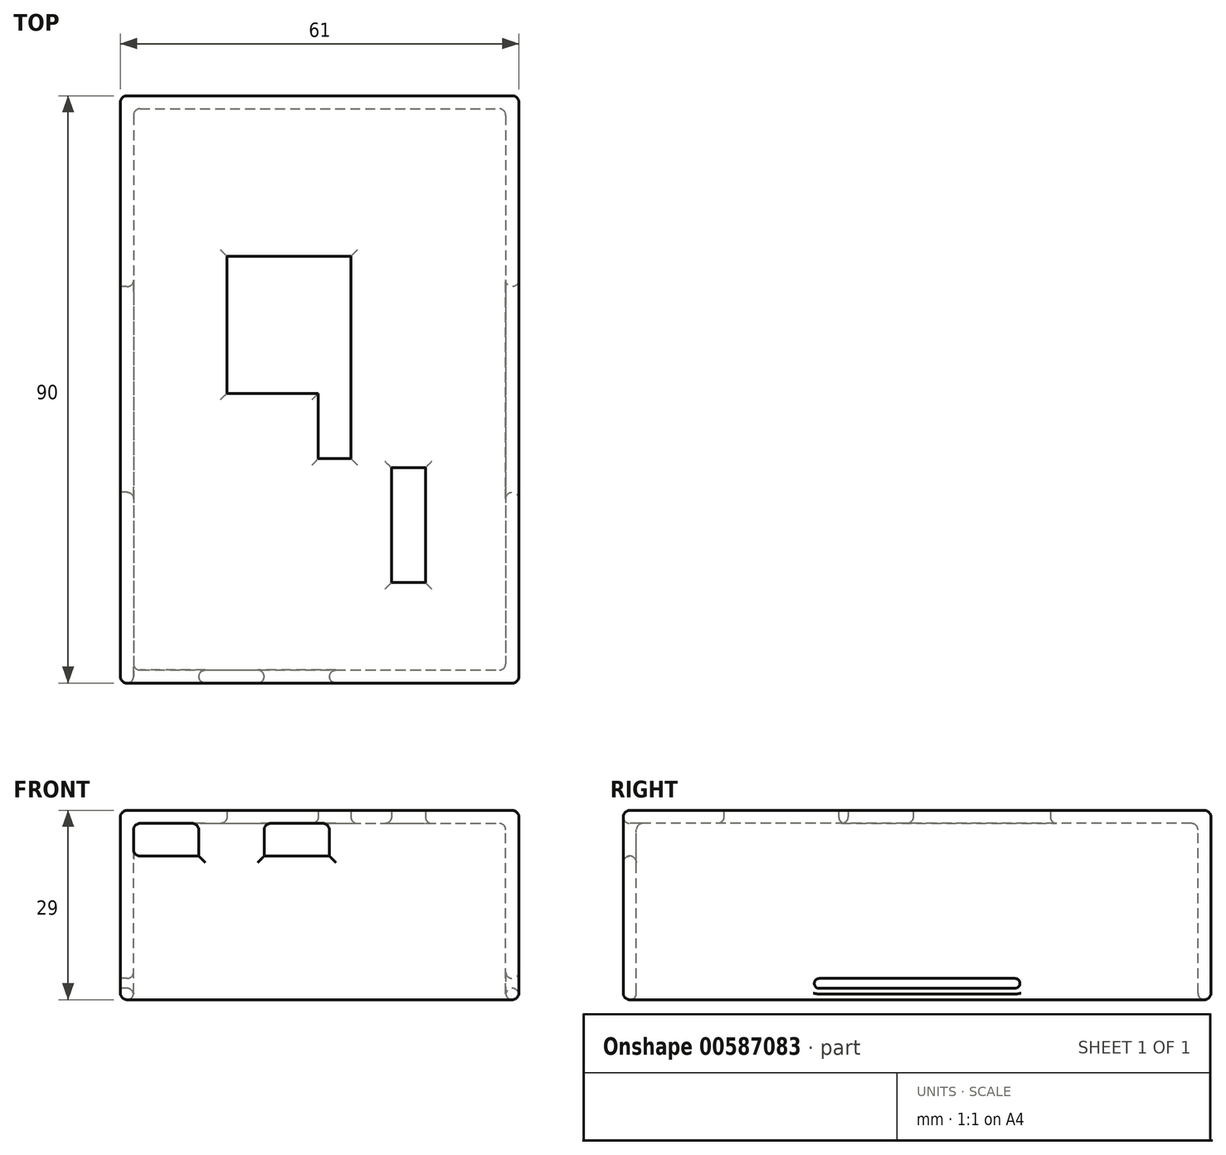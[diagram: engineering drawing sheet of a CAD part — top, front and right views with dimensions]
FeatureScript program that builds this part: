
annotation { "Feature Type Name" : "Feature", "Feature Type Description" : "" }
export const myFeature = defineFeature(function(context is Context, id is Id, definition is map)
    precondition{}
    {
        {
            var Q0;
            Q0=qCreatedBy(makeId("Top.planeOp"),FACE);
            var sketch = newSketch(context, id + "F0", { "sketchPlane" : qUnion([Q0])});
            skLineSegment(sketch, "E0.bottom", {"start": v(0, 0) * mm, "end": v(57, 0) * mm});
            skLineSegment(sketch, "E0.top", {"start": v(0, -86) * mm, "end": v(57, -86) * mm});
            skLineSegment(sketch, "E0.left", {"start": v(0, 0) * mm, "end": v(0, -86) * mm});
            skLineSegment(sketch, "E0.right", {"start": v(57, 0) * mm, "end": v(57, -86) * mm});
            skLineSegment(sketch, "E1.bottom", {"start": v(14.3, -22.6) * mm, "end": v(33.3, -22.6) * mm});
            skLineSegment(sketch, "E1.left", {"start": v(14.3, -22.6) * mm, "end": v(14.3, -43.6) * mm});
            skLineSegment(sketch, "E1.right", {"start": v(33.3, -22.6) * mm, "end": v(33.3, -43.6) * mm});
            skLineSegment(sketch, "E2", {"start": v(14.3, -22.6) * mm, "end": v(14.3, 0) * mm, "construction": true});
            skLineSegment(sketch, "E3", {"start": v(14.3, 0) * mm, "end": v(14.3, -22.6) * mm, "construction": true});
            skLineSegment(sketch, "E4", {"start": v(14.3, -22.6) * mm, "end": v(0, -22.6) * mm, "construction": true});
            skLineSegment(sketch, "E5.bottom", {"start": v(39.5, -55) * mm, "end": v(44.7, -55) * mm});
            skLineSegment(sketch, "E5.top", {"start": v(39.5, -72.6) * mm, "end": v(44.7, -72.6) * mm});
            skLineSegment(sketch, "E5.left", {"start": v(39.5, -55) * mm, "end": v(39.5, -72.6) * mm});
            skLineSegment(sketch, "E5.right", {"start": v(44.7, -55) * mm, "end": v(44.7, -72.6) * mm});
            skLineSegment(sketch, "E6", {"start": v(28.3, -43.6) * mm, "end": v(28.3, -53.6) * mm});
            skLineSegment(sketch, "E7", {"start": v(28.3, -53.6) * mm, "end": v(33.3, -53.6) * mm});
            skLineSegment(sketch, "E8", {"start": v(33.3, -53.6) * mm, "end": v(33.3, -43.6) * mm});
            skLineSegment(sketch, "E9", {"start": v(14.3, -43.6) * mm, "end": v(28.3, -43.6) * mm});
            skLineSegment(sketch, "E10", {"start": v(33.3, -43.6) * mm, "end": v(28.3, -43.6) * mm, "construction": true});
            skSolve(sketch);
        }
        {
            var Q0;
            Q0 = qSketchRegion(id + "F0", true);
            extrude(context, id + "F1", {"entities" : qUnion([Q0]), "depth" : 2 * mm, "offsetDistance" : 25 * mm});
        }
        {
            var Q0;
            Q0=makeQuery(id+"F1.opExtrude","CAP_FACE",FACE,{"disambiguationData":[OSD([sQuery(id+"F0.wireOp",EDGE,"E0.bottom"),sQuery(id+"F0.wireOp",EDGE,"E0.top"),sQuery(id+"F0.wireOp",EDGE,"E0.left"),sQuery(id+"F0.wireOp",EDGE,"E0.right"),sQuery(id+"F0.wireOp",EDGE,"E1.bottom"),sQuery(id+"F0.wireOp",EDGE,"E1.left"),sQuery(id+"F0.wireOp",EDGE,"E1.right"),sQuery(id+"F0.wireOp",EDGE,"E5.bottom"),sQuery(id+"F0.wireOp",EDGE,"E5.top"),sQuery(id+"F0.wireOp",EDGE,"E5.left"),sQuery(id+"F0.wireOp",EDGE,"E5.right"),sQuery(id+"F0.wireOp",EDGE,"E6"),sQuery(id+"F0.wireOp",EDGE,"E7"),sQuery(id+"F0.wireOp",EDGE,"E8"),sQuery(id+"F0.wireOp",EDGE,"E9")])],"isStart":false});
            var sketch = newSketch(context, id + "F2", { "sketchPlane" : qUnion([Q0])});
            skLineSegment(sketch, "E11.0", {"start": v(0, 0) * mm, "end": v(57, 0) * mm});
            skLineSegment(sketch, "E11.1", {"start": v(57, 0) * mm, "end": v(57, -86) * mm});
            skLineSegment(sketch, "E11.2", {"start": v(0, -86) * mm, "end": v(57, -86) * mm});
            skLineSegment(sketch, "E11.3", {"start": v(0, 0) * mm, "end": v(0, -86) * mm});
            skLineSegment(sketch, "E12.0", {"start": v(-2, 2) * mm, "end": v(59, 2) * mm});
            skLineSegment(sketch, "E12.1", {"start": v(-2, 2) * mm, "end": v(-2, -88) * mm});
            skLineSegment(sketch, "E12.2", {"start": v(-2, -88) * mm, "end": v(59, -88) * mm});
            skLineSegment(sketch, "E12.3", {"start": v(59, 2) * mm, "end": v(59, -88) * mm});
            skSolve(sketch);
        }
        {
            var Q0;
            Q0 = qSketchRegion(id + "F2", true);
            extrude(context, id + "F3", {"entities" : qUnion([Q0]), "operationType" : NewBodyOperationType.ADD, "oppositeDirection" : true, "depth" : 29 * mm, "offsetDistance" : 25 * mm});
        }
        {
            var Q0;
            Q0=makeQuery(id+"F3.opExtrude","SWEPT_FACE",FACE,{"disambiguationData":[OSD([sQuery(id+"F2.wireOp",EDGE,"E12.2")])]});
            var sketch = newSketch(context, id + "F4", { "sketchPlane" : qUnion([Q0])});
            skLineSegment(sketch, "E13.bottom", {"start": v(20, 0) * mm, "end": v(30, 0) * mm});
            skLineSegment(sketch, "E13.top", {"start": v(20, -5) * mm, "end": v(30, -5) * mm});
            skLineSegment(sketch, "E13.left", {"start": v(20, 0) * mm, "end": v(20, -5) * mm});
            skLineSegment(sketch, "E13.right", {"start": v(30, 0) * mm, "end": v(30, -5) * mm});
            skLineSegment(sketch, "E14.bottom", {"start": v(0, 0) * mm, "end": v(10, 0) * mm});
            skLineSegment(sketch, "E14.top", {"start": v(0, -5) * mm, "end": v(10, -5) * mm});
            skLineSegment(sketch, "E14.left", {"start": v(0, 0) * mm, "end": v(0, -5) * mm});
            skLineSegment(sketch, "E14.right", {"start": v(10, 0) * mm, "end": v(10, -5) * mm});
            skSolve(sketch);
        }
        {
            var Q0;
            Q0=makeQuery(id+"F4.imprint","IMPRINT",FACE,{"disambiguationData":[TD([[makeQuery(id+"F4.imprint","IMPRINT",EDGE,{"derivedFrom":sQuery(id+"F4.wireOp",EDGE,"E14.bottom")}),-1.0]])]});
            var Q1;
            Q1=makeQuery(id+"F4.imprint","IMPRINT",FACE,{"disambiguationData":[TD([[makeQuery(id+"F4.imprint","IMPRINT",EDGE,{"derivedFrom":sQuery(id+"F4.wireOp",EDGE,"E13.bottom")}),-1.0]])]});
            extrude(context, id + "F5", {"entities" : qUnion([Q0, Q1]), "operationType" : NewBodyOperationType.REMOVE, "endBound" : BoundingType.UP_TO_NEXT, "oppositeDirection" : true, "depth" : 25 * mm, "offsetDistance" : 25 * mm});
        }
        {
            var Q0;
            Q0=makeQuery(id+"F3.opExtrude","SWEPT_FACE",FACE,{"disambiguationData":[OSD([sQuery(id+"F2.wireOp",EDGE,"E12.1")])]});
            var sketch = newSketch(context, id + "F6", { "sketchPlane" : qUnion([Q0])});
            skLineSegment(sketch, "E15", {"start": v(43, -27) * mm, "end": v(43, -24.5) * mm, "construction": true});
            skLineSegment(sketch, "E16", {"start": v(28, -24.5) * mm, "end": v(58, -24.5) * mm, "construction": true});
            skArc(sketch, "E17.0.startCap", {"start": v(28, -25.25) * mm, "mid": v(27.25, -24.5) * mm, "end": v(28, -23.75) * mm});
            skArc(sketch, "E17.0.endCap", {"start": v(58, -23.75) * mm, "mid": v(58.75, -24.5) * mm, "end": v(58, -25.25) * mm});
            skLineSegment(sketch, "E17.0.left", {"start": v(28, -23.75) * mm, "end": v(58, -23.75) * mm});
            skLineSegment(sketch, "E17.0.right", {"start": v(28, -25.25) * mm, "end": v(58, -25.25) * mm});
            skSolve(sketch);
        }
        {
            var Q0;
            Q0 = qSketchRegion(id + "F6", true);
            extrude(context, id + "F7", {"entities" : qUnion([Q0]), "operationType" : NewBodyOperationType.REMOVE, "endBound" : BoundingType.THROUGH_ALL, "oppositeDirection" : true, "depth" : 25 * mm, "offsetDistance" : 25 * mm});
        }
        {
            var Q0;
            Q0=makeQuery(id+"F3.opExtrude","SWEPT_EDGE",EDGE,{"disambiguationData":[OSD([sQuery(id+"F2.wireOp",EDGE,"E12.1"),sQuery(id+"F2.wireOp",EDGE,"E12.2")])]});
            fillet(context, id + "F8", {"entities" : qUnion([Q0]), "radius" : 1 * mm, "tangentPropagation" : true, "allowEdgeOverflow" : false});
        }
        {
            var Q0;
            Q0=makeQuery(id+"F3.opExtrude","SWEPT_FACE",FACE,{"disambiguationData":[OSD([sQuery(id+"F2.wireOp",EDGE,"E12.2")])]});
            var Q1;
            Q1=makeQuery(id+"F3.opExtrude","SWEPT_FACE",FACE,{"disambiguationData":[OSD([sQuery(id+"F2.wireOp",EDGE,"E12.3")])]});
            var Q2;
            Q2=makeQuery(id+"F3.opExtrude","SWEPT_FACE",FACE,{"disambiguationData":[OSD([sQuery(id+"F2.wireOp",EDGE,"E12.0")])]});
            var Q3;
            Q3=makeQuery(id+"F5.boolean.opBoolean","MERGE",FACE,{"derivedFrom":[makeQuery(id+"F1.opExtrude","CAP_FACE",FACE,{"disambiguationData":[OSD([sQuery(id+"F0.wireOp",EDGE,"E0.bottom"),sQuery(id+"F0.wireOp",EDGE,"E0.top"),sQuery(id+"F0.wireOp",EDGE,"E0.left"),sQuery(id+"F0.wireOp",EDGE,"E0.right"),sQuery(id+"F0.wireOp",EDGE,"E1.bottom"),sQuery(id+"F0.wireOp",EDGE,"E1.left"),sQuery(id+"F0.wireOp",EDGE,"E1.right"),sQuery(id+"F0.wireOp",EDGE,"E5.bottom"),sQuery(id+"F0.wireOp",EDGE,"E5.top"),sQuery(id+"F0.wireOp",EDGE,"E5.left"),sQuery(id+"F0.wireOp",EDGE,"E5.right"),sQuery(id+"F0.wireOp",EDGE,"E6"),sQuery(id+"F0.wireOp",EDGE,"E7"),sQuery(id+"F0.wireOp",EDGE,"E8"),sQuery(id+"F0.wireOp",EDGE,"E9")])],"isStart":true}),makeQuery(id+"F5.opExtrude","SWEPT_FACE",FACE,{"disambiguationData":[OSD([sQuery(id+"F4.wireOp",EDGE,"E13.bottom")])]}),makeQuery(id+"F5.opExtrude","SWEPT_FACE",FACE,{"disambiguationData":[OSD([sQuery(id+"F4.wireOp",EDGE,"E14.bottom")])]})]});
            var Q4;
            Q4=makeQuery(id+"F5.boolean.opBoolean","MERGE",FACE,{"derivedFrom":[makeQuery(id+"F3.opExtrude","SWEPT_FACE",FACE,{"disambiguationData":[OSD([sQuery(id+"F2.wireOp",EDGE,"E11.3")])]}),makeQuery(id+"F5.opExtrude","SWEPT_FACE",FACE,{"disambiguationData":[OSD([sQuery(id+"F4.wireOp",EDGE,"E14.left")])]})]});
            var Q5;
            Q5=makeQuery(id+"F3.opExtrude","SWEPT_FACE",FACE,{"disambiguationData":[OSD([sQuery(id+"F2.wireOp",EDGE,"E11.0")])]});
            var Q6;
            Q6=makeQuery(id+"F3.opExtrude","SWEPT_FACE",FACE,{"disambiguationData":[OSD([sQuery(id+"F2.wireOp",EDGE,"E11.2")])]});
            var Q7;
            Q7=makeQuery(id+"F3.opExtrude","SWEPT_FACE",FACE,{"disambiguationData":[OSD([sQuery(id+"F2.wireOp",EDGE,"E11.1")])]});
            fillet(context, id + "F9", {"entities" : qUnion([Q0, Q1, Q2, Q3, Q4, Q5, Q6, Q7]), "radius" : 1 * mm, "tangentPropagation" : true, "allowEdgeOverflow" : false});
        }
    });
